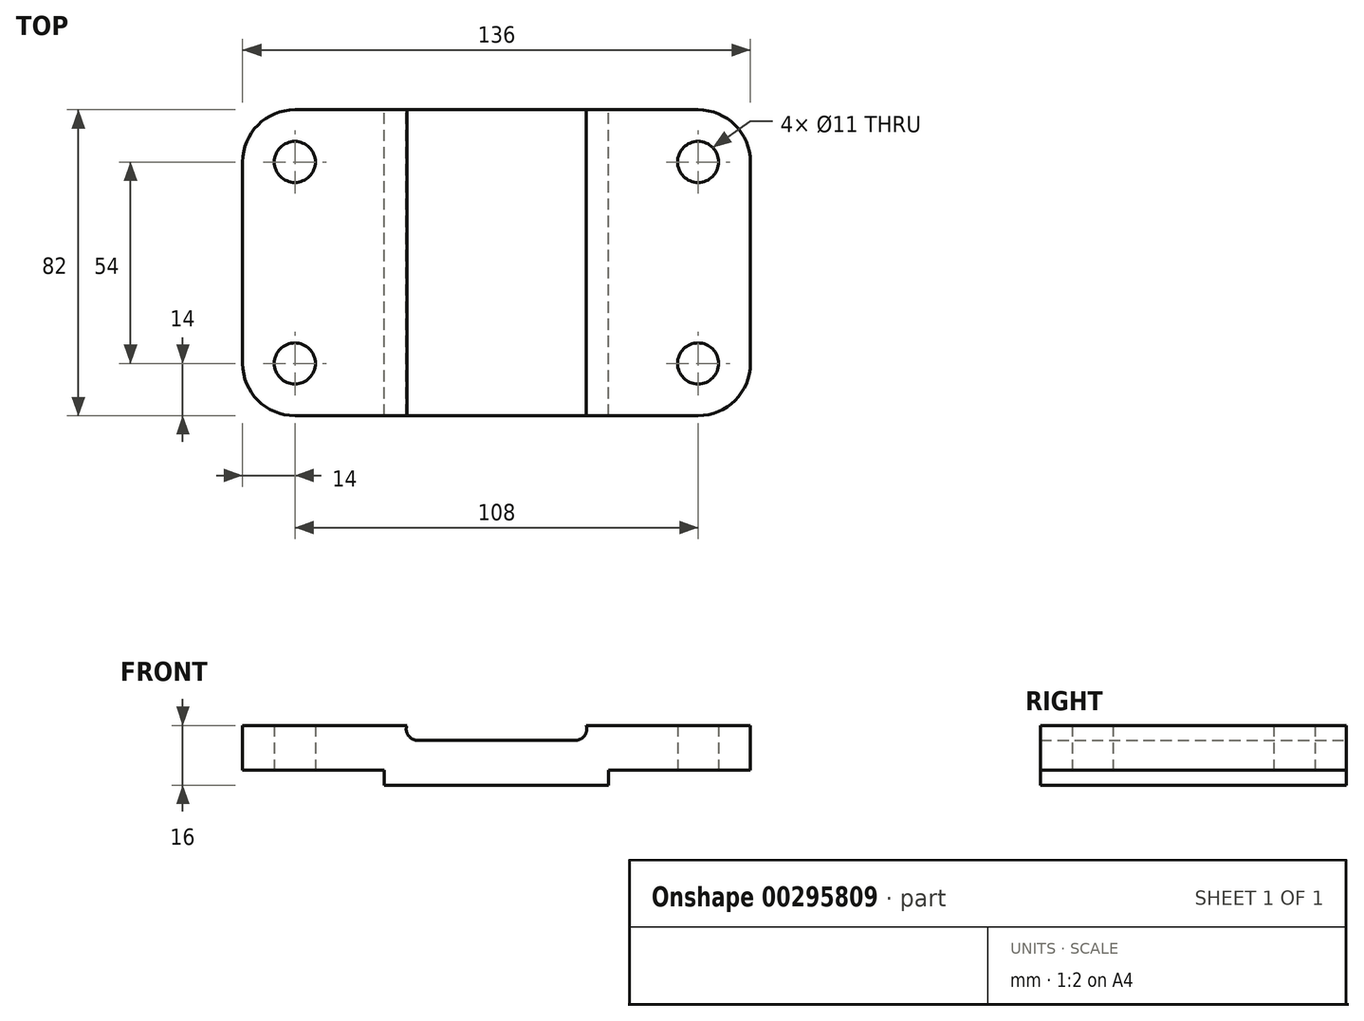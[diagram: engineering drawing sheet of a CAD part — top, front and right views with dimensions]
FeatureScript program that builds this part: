
annotation { "Feature Type Name" : "Feature", "Feature Type Description" : "" }
export const myFeature = defineFeature(function(context is Context, id is Id, definition is map)
    precondition{}
    {
        {
            var Q0;
            Q0=qCreatedBy(makeId("Front.planeOp"),FACE);
            var sketch = newSketch(context, id + "F0", { "sketchPlane" : qUnion([Q0])});
            skLineSegment(sketch, "E0", {"start": v(-30, 0) * mm, "end": v(30, 0) * mm});
            skLineSegment(sketch, "E1", {"start": v(30, 0) * mm, "end": v(30, 4) * mm});
            skLineSegment(sketch, "E2", {"start": v(30, 4) * mm, "end": v(68, 4) * mm});
            skLineSegment(sketch, "E3", {"start": v(68, 4) * mm, "end": v(68, 16) * mm});
            skLineSegment(sketch, "E4", {"start": v(68, 16) * mm, "end": v(24, 16) * mm});
            skLineSegment(sketch, "E5", {"start": v(-30, 0) * mm, "end": v(-30, 4) * mm});
            skLineSegment(sketch, "E6", {"start": v(-30, 4) * mm, "end": v(-68, 4) * mm});
            skLineSegment(sketch, "E7", {"start": v(-68, 4) * mm, "end": v(-68, 16) * mm});
            skLineSegment(sketch, "E8", {"start": v(-68, 16) * mm, "end": v(-24, 16) * mm});
            skArc(sketch, "E9", {"start": v(-24, 16) * mm, "mid": v(-23.62, 13.27) * mm, "end": v(-21.17, 12) * mm});
            skArc(sketch, "E10", {"start": v(21.17, 12) * mm, "mid": v(23.62, 13.27) * mm, "end": v(24, 16) * mm});
            skLineSegment(sketch, "E11", {"start": v(-21.17, 12) * mm, "end": v(21.17, 12) * mm});
            skSolve(sketch);
        }
        {
            var Q0;
            Q0 = qSketchRegion(id + "F0", true);
            extrude(context, id + "F1", {"entities" : qUnion([Q0]), "depth" : 82 * mm});
        }
        {
            var Q0;
            Q0=qCreatedBy(makeId("Top.planeOp"),FACE);
            var sketch = newSketch(context, id + "F2", { "sketchPlane" : qUnion([Q0])});
            skLineSegment(sketch, "E12", {"start": v(-54, 0) * mm, "end": v(54, 0) * mm});
            skCircle(sketch, "E13", {"center": v(-54, -14) * mm, "radius": 5.5 * mm});
            skLineSegment(sketch, "E14", {"start": v(68, -14) * mm, "end": v(68, -68) * mm});
            skArc(sketch, "E15", {"start": v(68, -14) * mm, "mid": v(63.9, -4.1) * mm, "end": v(54, 0) * mm});
            skArc(sketch, "E16", {"start": v(54, -82) * mm, "mid": v(63.9, -77.9) * mm, "end": v(68, -68) * mm});
            skArc(sketch, "E17", {"start": v(-54, 0) * mm, "mid": v(-63.9, -4.1) * mm, "end": v(-68, -14) * mm});
            skArc(sketch, "E18", {"start": v(-68, -68) * mm, "mid": v(-63.9, -77.9) * mm, "end": v(-54, -82) * mm});
            skCircle(sketch, "E19", {"center": v(54, -14) * mm, "radius": 5.5 * mm});
            skCircle(sketch, "E20", {"center": v(54, -68) * mm, "radius": 5.5 * mm});
            skCircle(sketch, "E21", {"center": v(-54, -68) * mm, "radius": 5.5 * mm});
            skLineSegment(sketch, "E22", {"start": v(-54, 0) * mm, "end": v(-68, 0) * mm});
            skLineSegment(sketch, "E23", {"start": v(-68, 0) * mm, "end": v(-68, -14) * mm});
            skLineSegment(sketch, "E24", {"start": v(54, 0) * mm, "end": v(68, 0) * mm});
            skLineSegment(sketch, "E25", {"start": v(68, -14) * mm, "end": v(68, 0) * mm});
            skLineSegment(sketch, "E26", {"start": v(-68, -68) * mm, "end": v(-68, -82) * mm});
            skLineSegment(sketch, "E27", {"start": v(-54, -82) * mm, "end": v(-68, -82) * mm});
            skLineSegment(sketch, "E28", {"start": v(54, -82) * mm, "end": v(68, -82) * mm});
            skLineSegment(sketch, "E29", {"start": v(68, -68) * mm, "end": v(68, -82) * mm});
            skSolve(sketch);
        }
        {
            var Q0;
            Q0 = qSketchRegion(id + "F2", true);
            extrude(context, id + "F3", {"entities" : qUnion([Q0]), "operationType" : NewBodyOperationType.REMOVE, "depth" : 16 * mm});
        }
    });
